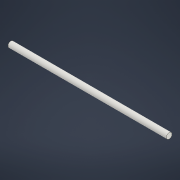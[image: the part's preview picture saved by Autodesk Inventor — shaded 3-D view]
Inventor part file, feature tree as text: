
AUTODESK INVENTOR PART (.ipt)
format: ipt  version: 2022 (Build 260153000, 153)  size: 86,528 bytes
history: native  units: in
note: dims shown in document units (in); Inventor stores cm internally (conversion verified against a paired STEP export)
features: extrude x1, sketch x1
ambient origin geometry x8: Origin, YZ Plane, XZ Plane, XY Plane, X Axis, Y Axis, Z Axis, Center Point
bodies: Solid1 (feature_tree)
feature tree (2):
  extrude  "Extrusion1"  Depth=3.3071in TaperAngle=0.0deg
  sketch  "Sketch1"  dims[d0=0.1181in d1=3.3071in d2=0.0in]
